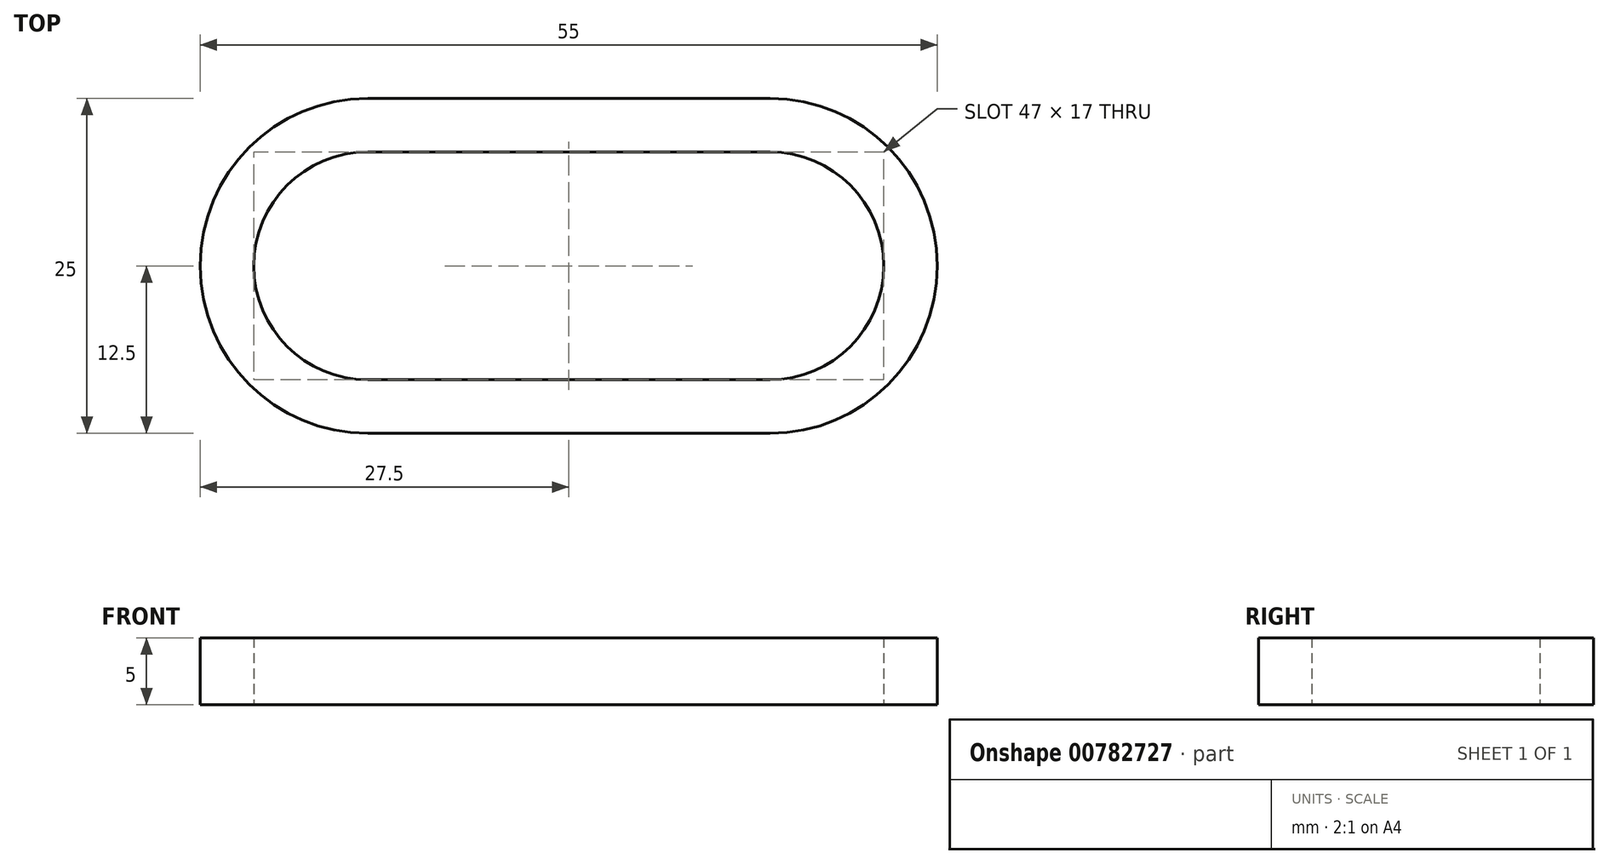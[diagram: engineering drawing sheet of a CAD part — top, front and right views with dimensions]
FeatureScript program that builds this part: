
annotation { "Feature Type Name" : "Feature", "Feature Type Description" : "" }
export const myFeature = defineFeature(function(context is Context, id is Id, definition is map)
    precondition{}
    {
        {
            var Q0;
            Q0=qCreatedBy(makeId("Top.planeOp"),FACE);
            var sketch = newSketch(context, id + "F0", { "sketchPlane" : qUnion([Q0])});
            skLineSegment(sketch, "E0.bottom", {"start": v(15, 12.5) * mm, "end": v(-15, 12.5) * mm});
            skLineSegment(sketch, "E0.top", {"start": v(15, -12.5) * mm, "end": v(-15, -12.5) * mm});
            skLineSegment(sketch, "E0.left", {"start": v(15, 12.5) * mm, "end": v(15, -12.5) * mm});
            skLineSegment(sketch, "E0.right", {"start": v(-15, 12.5) * mm, "end": v(-15, -12.5) * mm});
            skPoint(sketch, "E0.middle", {"position": v(0, 0) * mm});
            skCircle(sketch, "E1", {"center": v(15, 0) * mm, "radius": 12.5 * mm});
            skCircle(sketch, "E2", {"center": v(-15, 0) * mm, "radius": 12.5 * mm});
            skSolve(sketch);
        }
        {
            var Q0;
            {var subQ0=sQuery(id+"F0.wireOp",EDGE,"E0.right");Q0=makeQuery(id+"F0.imprint","IMPRINT",FACE,{"disambiguationData":[TD([[makeQuery(id+"F0.imprint","IMPRINT",EDGE,{"derivedFrom":subQ0}),-1.0]])]});}
            var Q1;
            {var subQ0=sQuery(id+"F0.wireOp",EDGE,"E0.right");Q1=makeQuery(id+"F0.imprint","IMPRINT",FACE,{"disambiguationData":[TD([[makeQuery(id+"F0.imprint","IMPRINT",EDGE,{"derivedFrom":subQ0}),1.0]])]});}
            var Q2;
            {var subQ0=sQuery(id+"F0.wireOp",EDGE,"E0.bottom");Q2=makeQuery(id+"F0.imprint","IMPRINT",FACE,{"disambiguationData":[TD([[makeQuery(id+"F0.imprint","IMPRINT",EDGE,{"derivedFrom":subQ0}),1.0]])]});}
            var Q3;
            {var subQ0=sQuery(id+"F0.wireOp",EDGE,"E0.left");Q3=makeQuery(id+"F0.imprint","IMPRINT",FACE,{"disambiguationData":[TD([[makeQuery(id+"F0.imprint","IMPRINT",EDGE,{"derivedFrom":subQ0}),-1.0]])]});}
            var Q4;
            {var subQ0=sQuery(id+"F0.wireOp",EDGE,"E0.left");Q4=makeQuery(id+"F0.imprint","IMPRINT",FACE,{"disambiguationData":[TD([[makeQuery(id+"F0.imprint","IMPRINT",EDGE,{"derivedFrom":subQ0}),1.0]])]});}
            var Q5;
            Q5=sQuery(id+"F0.wireOp",EDGE,"E2");
            extrude(context, id + "F1", {"entities" : qUnion([Q0, Q1, Q2, Q3, Q4]), "surfaceEntities" : qUnion([Q5]), "depth" : 5 * mm, "offsetDistance" : 25 * mm});
        }
        {
            var Q0;
            Q0=makeQuery(id+"F1.opExtrude","CAP_FACE",FACE,{"disambiguationData":[OSD([sQuery(id+"F0.wireOp",EDGE,"E0.bottom"),sQuery(id+"F0.wireOp",EDGE,"E0.top"),sQuery(id+"F0.wireOp",EDGE,"E1"),sQuery(id+"F0.wireOp",EDGE,"E2")])],"isStart":false});
            var Q1;
            Q1=makeQuery(id+"F1.opExtrude","CAP_FACE",FACE,{"disambiguationData":[OSD([sQuery(id+"F0.wireOp",EDGE,"E0.bottom"),sQuery(id+"F0.wireOp",EDGE,"E0.top"),sQuery(id+"F0.wireOp",EDGE,"E1"),sQuery(id+"F0.wireOp",EDGE,"E2")])],"isStart":true});
            shell(context, id + "F2", {"entities" : qUnion([Q0, Q1]), "thickness" : 4 * mm});
        }
    });
